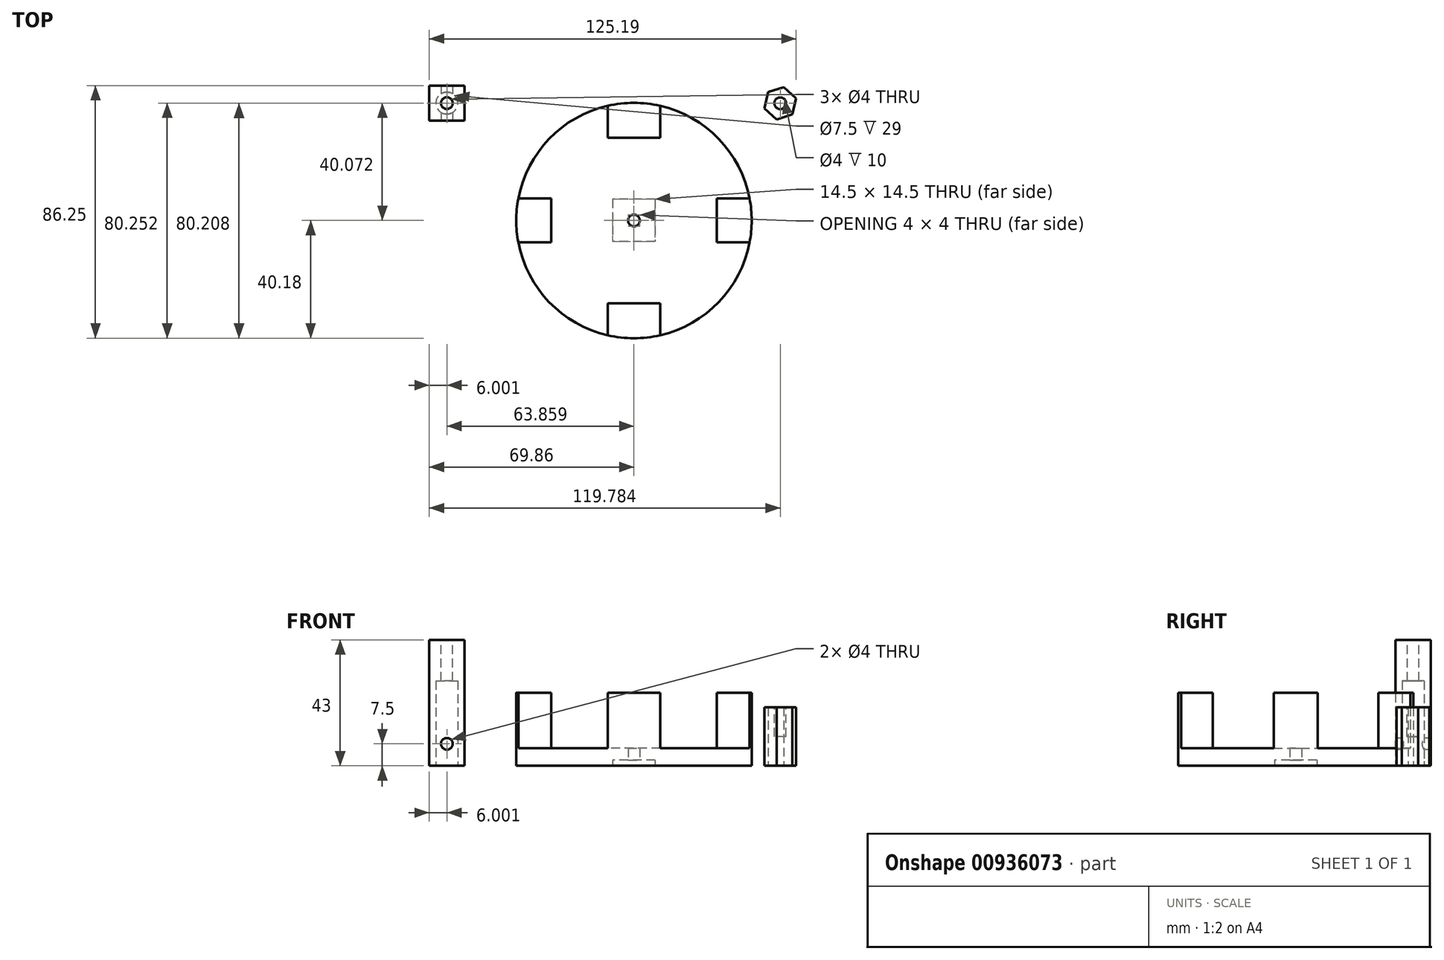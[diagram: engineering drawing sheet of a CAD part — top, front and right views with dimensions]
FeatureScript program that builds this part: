
annotation { "Feature Type Name" : "Feature", "Feature Type Description" : "" }
export const myFeature = defineFeature(function(context is Context, id is Id, definition is map)
    precondition{}
    {
        {
            var Q0;
            Q0=qCreatedBy(makeId("Top.planeOp"),FACE);
            var sketch = newSketch(context, id + "F0", { "sketchPlane" : qUnion([Q0])});
            skLineSegment(sketch, "E0.bottom", {"start": v(9, 28.25) * mm, "end": v(-9, 28.25) * mm});
            skLineSegment(sketch, "E0.top", {"start": v(9, 40.25) * mm, "end": v(-9, 40.25) * mm});
            skLineSegment(sketch, "E0.left", {"start": v(9, 28.25) * mm, "end": v(9, 40.25) * mm});
            skLineSegment(sketch, "E0.right", {"start": v(-9, 28.25) * mm, "end": v(-9, 40.25) * mm});
            skPoint(sketch, "E0.middle", {"position": v(0, 34.25) * mm});
            skLineSegment(sketch, "E1.bottom", {"start": v(9, -40.25) * mm, "end": v(-9, -40.25) * mm});
            skLineSegment(sketch, "E1.top", {"start": v(9, -28.25) * mm, "end": v(-9, -28.25) * mm});
            skLineSegment(sketch, "E1.left", {"start": v(9, -40.25) * mm, "end": v(9, -28.25) * mm});
            skLineSegment(sketch, "E1.right", {"start": v(-9, -40.25) * mm, "end": v(-9, -28.25) * mm});
            skPoint(sketch, "E1.middle", {"position": v(0, -34.25) * mm});
            skLineSegment(sketch, "E2.bottom", {"start": v(40.25, -7.5) * mm, "end": v(28.25, -7.5) * mm});
            skLineSegment(sketch, "E2.top", {"start": v(40.25, 7.5) * mm, "end": v(28.25, 7.5) * mm});
            skLineSegment(sketch, "E2.left", {"start": v(40.25, -7.5) * mm, "end": v(40.25, 7.5) * mm});
            skLineSegment(sketch, "E2.right", {"start": v(28.25, -7.5) * mm, "end": v(28.25, 7.5) * mm});
            skPoint(sketch, "E2.middle", {"position": v(34.25, 0) * mm});
            skLineSegment(sketch, "E3.bottom", {"start": v(-40.25, 7.5) * mm, "end": v(-28.25, 7.5) * mm});
            skLineSegment(sketch, "E3.top", {"start": v(-40.25, -7.5) * mm, "end": v(-28.25, -7.5) * mm});
            skLineSegment(sketch, "E3.left", {"start": v(-40.25, 7.5) * mm, "end": v(-40.25, -7.5) * mm});
            skLineSegment(sketch, "E3.right", {"start": v(-28.25, 7.5) * mm, "end": v(-28.25, -7.5) * mm});
            skPoint(sketch, "E3.middle", {"position": v(-34.25, 0) * mm});
            skCircle(sketch, "E4", {"center": v(0, 0) * mm, "radius": 40.18 * mm});
            skSolve(sketch);
        }
        {
            var Q0;
            {var subQ0=sQuery(id+"F0.wireOp",EDGE,"E3.right");Q0=makeQuery(id+"F0.imprint","IMPRINT",FACE,{"disambiguationData":[TD([[makeQuery(id+"F0.imprint","IMPRINT",EDGE,{"derivedFrom":subQ0}),-1.0]])]});}
            var Q1;
            {var subQ0=sQuery(id+"F0.wireOp",EDGE,"E0.bottom");Q1=makeQuery(id+"F0.imprint","IMPRINT",FACE,{"disambiguationData":[TD([[makeQuery(id+"F0.imprint","IMPRINT",EDGE,{"derivedFrom":subQ0}),-1.0]])]});}
            var Q2;
            {var subQ0=sQuery(id+"F0.wireOp",EDGE,"E2.right");Q2=makeQuery(id+"F0.imprint","IMPRINT",FACE,{"disambiguationData":[TD([[makeQuery(id+"F0.imprint","IMPRINT",EDGE,{"derivedFrom":subQ0}),-1.0]])]});}
            var Q3;
            {var subQ0=sQuery(id+"F0.wireOp",EDGE,"E1.top");Q3=makeQuery(id+"F0.imprint","IMPRINT",FACE,{"disambiguationData":[TD([[makeQuery(id+"F0.imprint","IMPRINT",EDGE,{"derivedFrom":subQ0}),1.0]])]});}
            extrude(context, id + "F1", {"entities" : qUnion([Q0, Q1, Q2, Q3]), "depth" : 25 * mm, "offsetDistance" : 25 * mm});
        }
        {
            var Q0;
            {var subQ10=sQuery(id+"F0.wireOp",EDGE,"E0.bottom");Q0=makeQuery(id+"F0.imprint","IMPRINT",FACE,{"disambiguationData":[TD([[makeQuery(id+"F0.imprint","IMPRINT",EDGE,{"derivedFrom":subQ10}),1.0]])]});}
            extrude(context, id + "F2", {"entities" : qUnion([Q0]), "operationType" : NewBodyOperationType.ADD, "depth" : 6 * mm, "offsetDistance" : 25 * mm});
        }
        {
            var Q0;
            {var subQ0=sQuery(id+"F0.wireOp",EDGE,"E4");var subQ1=sQuery(id+"F0.wireOp",EDGE,"E3.right");var subQ2=sQuery(id+"F0.wireOp",EDGE,"E3.top");var subQ3=sQuery(id+"F0.wireOp",EDGE,"E3.bottom");var subQ4=sQuery(id+"F0.wireOp",EDGE,"E2.right");var subQ5=sQuery(id+"F0.wireOp",EDGE,"E2.top");var subQ6=sQuery(id+"F0.wireOp",EDGE,"E2.bottom");var subQ7=sQuery(id+"F0.wireOp",EDGE,"E1.right");var subQ8=sQuery(id+"F0.wireOp",EDGE,"E1.left");var subQ9=sQuery(id+"F0.wireOp",EDGE,"E1.top");var subQ10=sQuery(id+"F0.wireOp",EDGE,"E0.right");var subQ11=sQuery(id+"F0.wireOp",EDGE,"E0.left");var subQ12=sQuery(id+"F0.wireOp",EDGE,"E0.bottom");Q0=makeQuery(id+"F2.boolean.opBoolean","MERGE",FACE,{"derivedFrom":[makeQuery(id+"F1.opExtrude","CAP_FACE",FACE,{"disambiguationData":[OSD([subQ12,subQ11,subQ10,subQ0])],"isStart":true}),makeQuery(id+"F1.opExtrude","CAP_FACE",FACE,{"disambiguationData":[OSD([subQ9,subQ8,subQ7,subQ0])],"isStart":true}),makeQuery(id+"F1.opExtrude","CAP_FACE",FACE,{"disambiguationData":[OSD([subQ6,subQ5,subQ4,subQ0])],"isStart":true}),makeQuery(id+"F1.opExtrude","CAP_FACE",FACE,{"disambiguationData":[OSD([subQ3,subQ2,subQ1,subQ0])],"isStart":true}),makeQuery(id+"F2.opExtrude","CAP_FACE",FACE,{"disambiguationData":[OSD([subQ12,subQ11,subQ10,subQ9,subQ8,subQ7,subQ6,subQ5,subQ4,subQ3,subQ2,subQ1,subQ0])],"isStart":true})]});}
            var sketch = newSketch(context, id + "F3", { "sketchPlane" : qUnion([Q0])});
            skCircle(sketch, "E5", {"center": v(0, 0) * mm, "radius": 2 * mm});
            skSolve(sketch);
        }
        {
            var Q0;
            Q0=qCreatedBy(makeId("Top.planeOp"),FACE);
            var sketch = newSketch(context, id + "F4", { "sketchPlane" : qUnion([Q0])});
            skCircle(sketch, "E6.cCircle", {"center": v(49.92, 40.03) * mm, "radius": 5.67 * mm, "construction": true});
            skLineSegment(sketch, "E6.0", {"start": v(54.11, 36.2) * mm, "end": v(48.7, 34.49) * mm});
            skLineSegment(sketch, "E6.1", {"start": v(48.7, 34.49) * mm, "end": v(44.52, 38.31) * mm});
            skLineSegment(sketch, "E6.2", {"start": v(44.52, 38.31) * mm, "end": v(45.73, 43.85) * mm});
            skLineSegment(sketch, "E6.3", {"start": v(45.73, 43.85) * mm, "end": v(51.14, 45.57) * mm});
            skLineSegment(sketch, "E6.4", {"start": v(51.14, 45.57) * mm, "end": v(55.33, 41.74) * mm});
            skLineSegment(sketch, "E6.5", {"start": v(55.33, 41.74) * mm, "end": v(54.11, 36.2) * mm});
            skSolve(sketch);
        }
        {
            var Q0;
            Q0=makeQuery(id+"F4.imprint","IMPRINT",FACE,{"disambiguationData":[TD([[makeQuery(id+"F4.imprint","IMPRINT",EDGE,{"derivedFrom":sQuery(id+"F4.wireOp",EDGE,"E6.0")}),-1.0]])]});
            extrude(context, id + "F5", {"entities" : qUnion([Q0]), "depth" : 20 * mm, "offsetDistance" : 25 * mm});
        }
        {
            var Q0;
            Q0=makeQuery(id+"F5.opExtrude","CAP_FACE",FACE,{"disambiguationData":[OSD([sQuery(id+"F4.wireOp",EDGE,"E6.0"),sQuery(id+"F4.wireOp",EDGE,"E6.1"),sQuery(id+"F4.wireOp",EDGE,"E6.2"),sQuery(id+"F4.wireOp",EDGE,"E6.3"),sQuery(id+"F4.wireOp",EDGE,"E6.4"),sQuery(id+"F4.wireOp",EDGE,"E6.5")])],"isStart":false});
            var sketch = newSketch(context, id + "F6", { "sketchPlane" : qUnion([Q0])});
            skCircle(sketch, "E7", {"center": v(49.92, 40.03) * mm, "radius": 2 * mm});
            skLineSegment(sketch, "E8", {"start": v(51.14, 45.57) * mm, "end": v(48.7, 34.49) * mm, "construction": true});
            skLineSegment(sketch, "E9", {"start": v(45.13, 41.08) * mm, "end": v(54.72, 38.97) * mm, "construction": true});
            skSolve(sketch);
        }
        {
            var Q0;
            Q0=makeQuery(id+"F6.imprint","IMPRINT",FACE,{"disambiguationData":[TD([[makeQuery(id+"F6.imprint","IMPRINT",EDGE,{"derivedFrom":sQuery(id+"F6.wireOp",EDGE,"E7")}),1.0]])]});
            extrude(context, id + "F7", {"entities" : qUnion([Q0]), "operationType" : NewBodyOperationType.REMOVE, "oppositeDirection" : true, "depth" : 10 * mm, "offsetDistance" : 25 * mm});
        }
        {
            var Q0;
            Q0=makeQuery(id+"F1.opExtrude","SWEPT_BODY",BODY,{"disambiguationData":[OSD([sQuery(id+"F0.wireOp",EDGE,"E0.bottom"),sQuery(id+"F0.wireOp",EDGE,"E0.left"),sQuery(id+"F0.wireOp",EDGE,"E0.right"),sQuery(id+"F0.wireOp",EDGE,"E4")])]});
            transform(context, id + "F8", {"entities" : qUnion([Q0]), "transformType" : TransformType.TRANSLATION_3D, "dx" : 0 * mm, "dy" : 0 * mm, "dz" : 0 * mm, "makeCopy" : true});
        }
        {
            var Q0;
            Q0=makeQuery(id+"F3.imprint","IMPRINT",FACE,{"disambiguationData":[TD([[makeQuery(id+"F3.imprint","IMPRINT",EDGE,{"derivedFrom":sQuery(id+"F3.wireOp",EDGE,"E5")}),1.0]])]});
            extrude(context, id + "F9", {"entities" : qUnion([Q0]), "operationType" : NewBodyOperationType.REMOVE, "oppositeDirection" : true, "depth" : 25 * mm, "offsetDistance" : 25 * mm});
        }
        {
            var Q0;
            {var subQ0=sQuery(id+"F0.wireOp",EDGE,"E4");var subQ1=sQuery(id+"F0.wireOp",EDGE,"E3.right");var subQ2=sQuery(id+"F0.wireOp",EDGE,"E3.top");var subQ3=sQuery(id+"F0.wireOp",EDGE,"E3.bottom");var subQ4=sQuery(id+"F0.wireOp",EDGE,"E2.right");var subQ5=sQuery(id+"F0.wireOp",EDGE,"E2.top");var subQ6=sQuery(id+"F0.wireOp",EDGE,"E2.bottom");var subQ7=sQuery(id+"F0.wireOp",EDGE,"E1.right");var subQ8=sQuery(id+"F0.wireOp",EDGE,"E1.left");var subQ9=sQuery(id+"F0.wireOp",EDGE,"E1.top");var subQ10=sQuery(id+"F0.wireOp",EDGE,"E0.right");var subQ11=sQuery(id+"F0.wireOp",EDGE,"E0.left");var subQ12=sQuery(id+"F0.wireOp",EDGE,"E0.bottom");Q0=makeQuery(id+"F2.boolean.opBoolean","MERGE",FACE,{"derivedFrom":[makeQuery(id+"F1.opExtrude","CAP_FACE",FACE,{"disambiguationData":[OSD([subQ12,subQ11,subQ10,subQ0])],"isStart":true}),makeQuery(id+"F1.opExtrude","CAP_FACE",FACE,{"disambiguationData":[OSD([subQ9,subQ8,subQ7,subQ0])],"isStart":true}),makeQuery(id+"F1.opExtrude","CAP_FACE",FACE,{"disambiguationData":[OSD([subQ6,subQ5,subQ4,subQ0])],"isStart":true}),makeQuery(id+"F1.opExtrude","CAP_FACE",FACE,{"disambiguationData":[OSD([subQ3,subQ2,subQ1,subQ0])],"isStart":true}),makeQuery(id+"F2.opExtrude","CAP_FACE",FACE,{"disambiguationData":[OSD([subQ12,subQ11,subQ10,subQ9,subQ8,subQ7,subQ6,subQ5,subQ4,subQ3,subQ2,subQ1,subQ0])],"isStart":true})]});}
            var sketch = newSketch(context, id + "F10", { "sketchPlane" : qUnion([Q0])});
            skLineSegment(sketch, "E10.bottom", {"start": v(7.25, -7.25) * mm, "end": v(-7.25, -7.25) * mm});
            skLineSegment(sketch, "E10.top", {"start": v(7.25, 7.25) * mm, "end": v(-7.25, 7.25) * mm});
            skLineSegment(sketch, "E10.left", {"start": v(7.25, -7.25) * mm, "end": v(7.25, 7.25) * mm});
            skLineSegment(sketch, "E10.right", {"start": v(-7.25, -7.25) * mm, "end": v(-7.25, 7.25) * mm});
            skPoint(sketch, "E10.middle", {"position": v(0, 0) * mm});
            skSolve(sketch);
        }
        {
            var Q0;
            Q0=makeQuery(id+"F10.imprint","IMPRINT",FACE,{"disambiguationData":[TD([[makeQuery(id+"F10.imprint","IMPRINT",EDGE,{"derivedFrom":sQuery(id+"F10.wireOp",EDGE,"E10.bottom")}),-1.0]])]});
            extrude(context, id + "F11", {"entities" : qUnion([Q0]), "operationType" : NewBodyOperationType.REMOVE, "oppositeDirection" : true, "depth" : 2 * mm, "offsetDistance" : 25 * mm});
        }
        {
            var Q0;
            Q0=qCreatedBy(makeId("Top.planeOp"),FACE);
            var sketch = newSketch(context, id + "F12", { "sketchPlane" : qUnion([Q0])});
            skLineSegment(sketch, "E11.bottom", {"start": v(-57.86, 34.07) * mm, "end": v(-69.86, 34.07) * mm});
            skLineSegment(sketch, "E11.top", {"start": v(-57.86, 46.07) * mm, "end": v(-69.86, 46.07) * mm});
            skLineSegment(sketch, "E11.left", {"start": v(-57.86, 34.07) * mm, "end": v(-57.86, 46.07) * mm});
            skLineSegment(sketch, "E11.right", {"start": v(-69.86, 34.07) * mm, "end": v(-69.86, 46.07) * mm});
            skPoint(sketch, "E11.middle", {"position": v(-63.86, 40.07) * mm});
            skSolve(sketch);
        }
        {
            var Q0;
            Q0=makeQuery(id+"F12.imprint","IMPRINT",FACE,{"disambiguationData":[TD([[makeQuery(id+"F12.imprint","IMPRINT",EDGE,{"derivedFrom":sQuery(id+"F12.wireOp",EDGE,"E11.bottom")}),-1.0]])]});
            extrude(context, id + "F13", {"entities" : qUnion([Q0]), "depth" : 43 * mm, "offsetDistance" : 25 * mm});
        }
        {
            var Q0;
            Q0=makeQuery(id+"F13.opExtrude","CAP_FACE",FACE,{"disambiguationData":[OSD([sQuery(id+"F12.wireOp",EDGE,"E11.bottom"),sQuery(id+"F12.wireOp",EDGE,"E11.top"),sQuery(id+"F12.wireOp",EDGE,"E11.left"),sQuery(id+"F12.wireOp",EDGE,"E11.right")])],"isStart":false});
            var sketch = newSketch(context, id + "F14", { "sketchPlane" : qUnion([Q0])});
            skCircle(sketch, "E12", {"center": v(-63.86, 40.07) * mm, "radius": 2 * mm});
            skPoint(sketch, "E12.centerSnap0", {"position": v(-63.86, 46.07) * mm});
            skPoint(sketch, "E12.centerSnap1", {"position": v(-69.86, 40.07) * mm});
            skSolve(sketch);
        }
        {
            var Q0;
            Q0=makeQuery(id+"F14.imprint","IMPRINT",FACE,{"disambiguationData":[TD([[makeQuery(id+"F14.imprint","IMPRINT",EDGE,{"derivedFrom":sQuery(id+"F14.wireOp",EDGE,"E12")}),1.0]])]});
            extrude(context, id + "F15", {"entities" : qUnion([Q0]), "operationType" : NewBodyOperationType.REMOVE, "oppositeDirection" : true, "depth" : 14 * mm, "offsetDistance" : 25 * mm});
        }
        {
            var Q0;
            Q0=makeQuery(id+"F13.opExtrude","CAP_FACE",FACE,{"disambiguationData":[OSD([sQuery(id+"F12.wireOp",EDGE,"E11.bottom"),sQuery(id+"F12.wireOp",EDGE,"E11.top"),sQuery(id+"F12.wireOp",EDGE,"E11.left"),sQuery(id+"F12.wireOp",EDGE,"E11.right")])],"isStart":true});
            var sketch = newSketch(context, id + "F16", { "sketchPlane" : qUnion([Q0])});
            skCircle(sketch, "E13", {"center": v(-63.86, -40.07) * mm, "radius": 3.75 * mm});
            skPoint(sketch, "E13.centerSnap0", {"position": v(-63.86, -34.07) * mm});
            skPoint(sketch, "E13.centerSnap1", {"position": v(-69.86, -40.07) * mm});
            skSolve(sketch);
        }
        {
            var Q0;
            Q0=makeQuery(id+"F16.imprint","IMPRINT",FACE,{"disambiguationData":[TD([[makeQuery(id+"F16.imprint","IMPRINT",EDGE,{"derivedFrom":sQuery(id+"F16.wireOp",EDGE,"E13")}),1.0]])]});
            extrude(context, id + "F17", {"entities" : qUnion([Q0]), "operationType" : NewBodyOperationType.REMOVE, "oppositeDirection" : true, "depth" : 29 * mm, "offsetDistance" : 25 * mm});
        }
        {
            var Q0;
            Q0=makeQuery(id+"F13.opExtrude","SWEPT_FACE",FACE,{"disambiguationData":[OSD([sQuery(id+"F12.wireOp",EDGE,"E11.bottom")])]});
            var sketch = newSketch(context, id + "F18", { "sketchPlane" : qUnion([Q0])});
            skCircle(sketch, "E14", {"center": v(-63.86, 7.5) * mm, "radius": 2 * mm});
            skPoint(sketch, "E14.centerSnap0", {"position": v(-63.86, 0) * mm});
            skSolve(sketch);
        }
        {
            var Q0;
            Q0=makeQuery(id+"F18.imprint","IMPRINT",FACE,{"disambiguationData":[TD([[makeQuery(id+"F18.imprint","IMPRINT",EDGE,{"derivedFrom":sQuery(id+"F18.wireOp",EDGE,"E14")}),1.0]])]});
            extrude(context, id + "F19", {"entities" : qUnion([Q0]), "operationType" : NewBodyOperationType.REMOVE, "oppositeDirection" : true, "depth" : 20 * mm, "offsetDistance" : 25 * mm});
        }
    });
